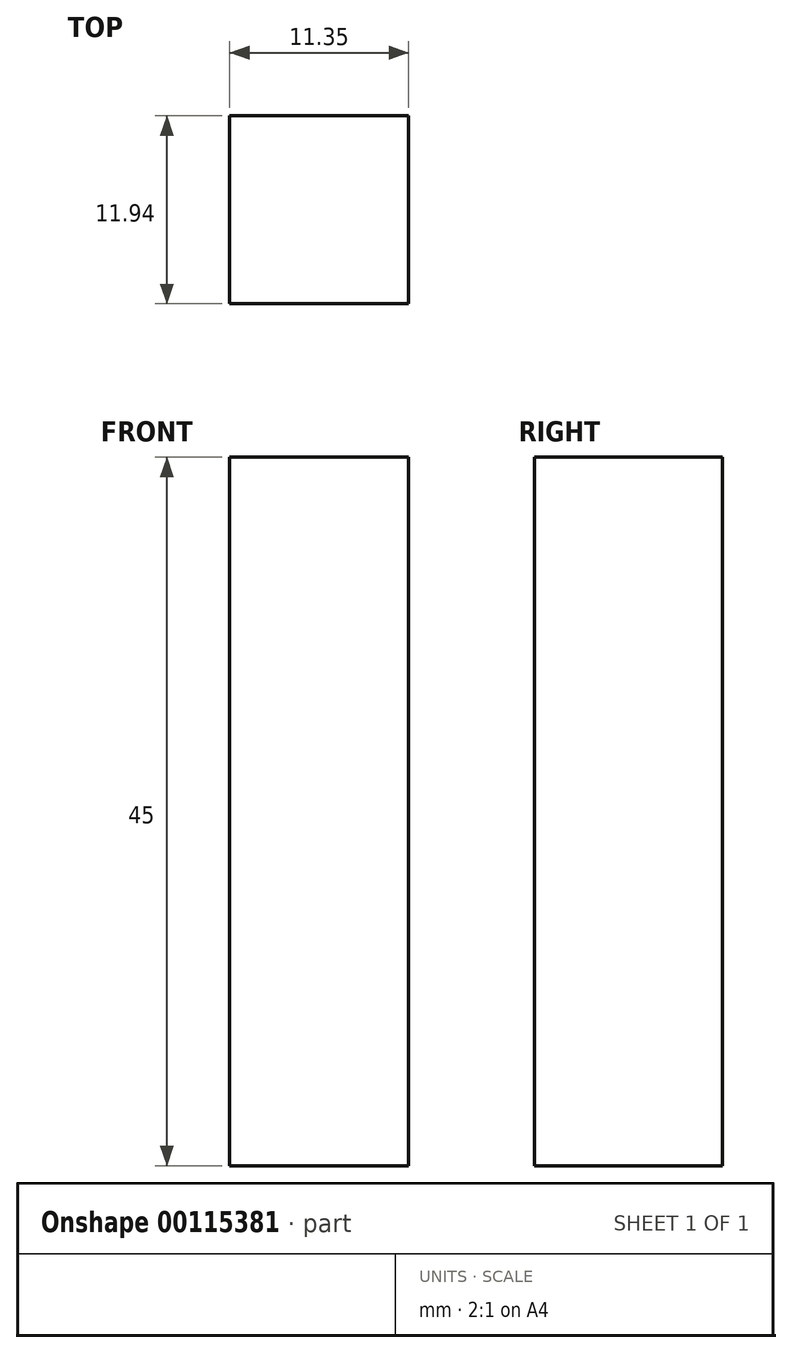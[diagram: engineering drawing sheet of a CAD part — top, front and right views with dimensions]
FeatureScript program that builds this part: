
annotation { "Feature Type Name" : "Feature", "Feature Type Description" : "" }
export const myFeature = defineFeature(function(context is Context, id is Id, definition is map)
    precondition{}
    {
        {
            var Q0;
            Q0=qCreatedBy(makeId("Top.planeOp"),FACE);
            var sketch = newSketch(context, id + "F0", { "sketchPlane" : qUnion([Q0])});
            skLineSegment(sketch, "E0.bottom", {"start": v(0, 0) * mm, "end": v(11.35, 0) * mm});
            skLineSegment(sketch, "E0.top", {"start": v(0, 11.94) * mm, "end": v(11.35, 11.94) * mm});
            skLineSegment(sketch, "E0.left", {"start": v(0, 0) * mm, "end": v(0, 11.94) * mm});
            skLineSegment(sketch, "E0.right", {"start": v(11.35, 0) * mm, "end": v(11.35, 11.94) * mm});
            skSolve(sketch);
        }
        {
            var Q0;
            Q0 = qSketchRegion(id + "F0", true);
            extrude(context, id + "F1", {"entities" : qUnion([Q0]), "depth" : 45 * mm});
        }
    });
